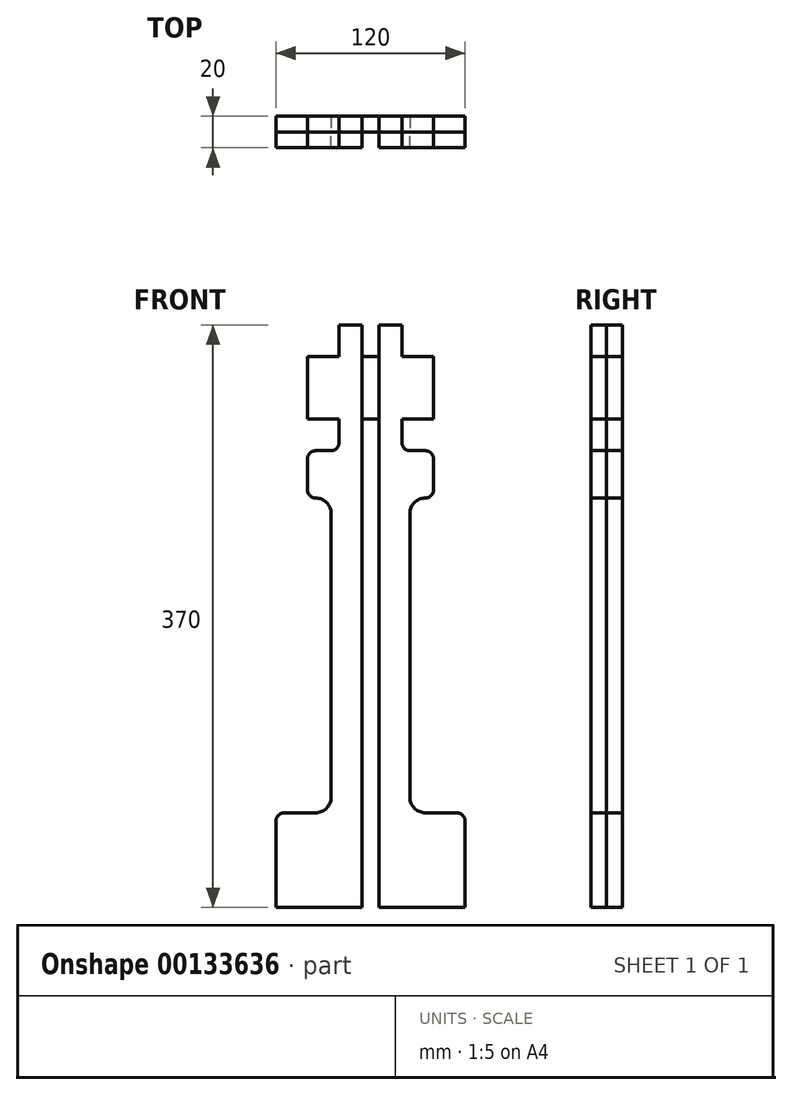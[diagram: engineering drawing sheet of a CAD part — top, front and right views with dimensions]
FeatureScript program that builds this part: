
annotation { "Feature Type Name" : "Feature", "Feature Type Description" : "" }
export const myFeature = defineFeature(function(context is Context, id is Id, definition is map)
    precondition{}
    {
        {
            var Q0;
            Q0=qCreatedBy(makeId("Front.planeOp"),FACE);
            var sketch = newSketch(context, id + "F0", { "sketchPlane" : qUnion([Q0])});
            skLineSegment(sketch, "E0.bottom", {"start": v(60, -30) * mm, "end": v(-60, -30) * mm});
            skLineSegment(sketch, "E0.top", {"start": v(55, 30) * mm, "end": v(35, 30) * mm});
            skLineSegment(sketch, "E0.left", {"start": v(60, -30) * mm, "end": v(60, 25) * mm});
            skLineSegment(sketch, "E0.right", {"start": v(-60, -30) * mm, "end": v(-60, 25) * mm});
            skPoint(sketch, "E0.middle", {"position": v(0, 0) * mm});
            skLineSegment(sketch, "E1.left", {"start": v(25, 40) * mm, "end": v(25, 220) * mm});
            skLineSegment(sketch, "E1.right", {"start": v(-25, 40) * mm, "end": v(-25, 220) * mm});
            skLineSegment(sketch, "E2.bottom", {"start": v(35, 230) * mm, "end": v(35, 230) * mm});
            skLineSegment(sketch, "E2.top", {"start": v(-25, 260) * mm, "end": v(-35, 260) * mm});
            skLineSegment(sketch, "E2.left", {"start": v(40, 235) * mm, "end": v(40, 255) * mm});
            skLineSegment(sketch, "E2.right", {"start": v(-40, 235) * mm, "end": v(-40, 255) * mm});
            skPoint(sketch, "E2.middle", {"position": v(0, 245) * mm});
            skLineSegment(sketch, "E3.top", {"start": v(20, 340) * mm, "end": v(-20, 340) * mm});
            skLineSegment(sketch, "E3.left", {"start": v(20, 265) * mm, "end": v(20, 340) * mm});
            skLineSegment(sketch, "E3.right", {"start": v(-20, 265) * mm, "end": v(-20, 340) * mm});
            skPoint(sketch, "E3.middle", {"position": v(0, 300) * mm});
            skLineSegment(sketch, "E4.bottom", {"start": v(40, 320) * mm, "end": v(-40, 320) * mm});
            skLineSegment(sketch, "E4.top", {"start": v(40, 280) * mm, "end": v(-40, 280) * mm});
            skLineSegment(sketch, "E4.left", {"start": v(40, 320) * mm, "end": v(40, 280) * mm});
            skLineSegment(sketch, "E4.right", {"start": v(-40, 320) * mm, "end": v(-40, 280) * mm});
            skLineSegment(sketch, "E5.bottom", {"start": v(5.5, -30) * mm, "end": v(-5.5, -30) * mm});
            skLineSegment(sketch, "E5.top", {"start": v(5.5, 160) * mm, "end": v(-5.5, 160) * mm});
            skLineSegment(sketch, "E5.left", {"start": v(5.5, -30) * mm, "end": v(5.5, 160) * mm});
            skLineSegment(sketch, "E5.right", {"start": v(-5.5, -30) * mm, "end": v(-5.5, 160) * mm});
            skPoint(sketch, "E5.middle", {"position": v(0, 65) * mm});
            skLineSegment(sketch, "E6.bottom", {"start": v(-5.5, 160) * mm, "end": v(5.5, 160) * mm});
            skLineSegment(sketch, "E6.top", {"start": v(-5.5, 340) * mm, "end": v(5.5, 340) * mm});
            skLineSegment(sketch, "E6.left", {"start": v(-5.5, 160) * mm, "end": v(-5.5, 340) * mm});
            skLineSegment(sketch, "E6.right", {"start": v(5.5, 160) * mm, "end": v(5.5, 340) * mm});
            skPoint(sketch, "E7.newPointA", {"position": v(-60, 30) * mm});
            skPoint(sketch, "E7.newPointB", {"position": v(25, 30) * mm});
            skArc(sketch, "E7.filletArc", {"start": v(25, 40) * mm, "mid": v(27.93, 32.93) * mm, "end": v(35, 30) * mm});
            skLineSegment(sketch, "E8", {"start": v(-55, 30) * mm, "end": v(-35, 30) * mm});
            skPoint(sketch, "E9.visualSharp", {"position": v(-25, 30) * mm});
            skArc(sketch, "E9.filletArc", {"start": v(-35, 30) * mm, "mid": v(-27.93, 32.93) * mm, "end": v(-25, 40) * mm});
            skArc(sketch, "E10.filletArc", {"start": v(-55, 30) * mm, "mid": v(-58.54, 28.54) * mm, "end": v(-60, 25) * mm});
            skPoint(sketch, "E11.visualSharp", {"position": v(60, 30) * mm});
            skArc(sketch, "E11.filletArc", {"start": v(60, 25) * mm, "mid": v(58.54, 28.54) * mm, "end": v(55, 30) * mm});
            skPoint(sketch, "E12.newPointA", {"position": v(25, 230) * mm});
            skPoint(sketch, "E12.newPointB", {"position": v(-40, 230) * mm});
            skArc(sketch, "E12.filletArc", {"start": v(35, 230) * mm, "mid": v(27.93, 227.07) * mm, "end": v(25, 220) * mm});
            skLineSegment(sketch, "E13", {"start": v(-35, 230) * mm, "end": v(-35, 230) * mm});
            skPoint(sketch, "E14.visualSharp", {"position": v(-25, 230) * mm});
            skArc(sketch, "E14.filletArc", {"start": v(-25, 220) * mm, "mid": v(-27.93, 227.07) * mm, "end": v(-35, 230) * mm});
            skPoint(sketch, "E15.newPointB", {"position": v(40, 260) * mm});
            skArc(sketch, "E15.filletArc", {"start": v(-25, 260) * mm, "mid": v(-21.46, 261.46) * mm, "end": v(-20, 265) * mm});
            skPoint(sketch, "E16.visualSharp", {"position": v(-40, 260) * mm});
            skArc(sketch, "E16.filletArc", {"start": v(-35, 260) * mm, "mid": v(-38.54, 258.54) * mm, "end": v(-40, 255) * mm});
            skArc(sketch, "E17.filletArc", {"start": v(-40, 235) * mm, "mid": v(-38.54, 231.46) * mm, "end": v(-35, 230) * mm});
            skPoint(sketch, "E18.visualSharp", {"position": v(40, 230) * mm});
            skArc(sketch, "E18.filletArc", {"start": v(35, 230) * mm, "mid": v(38.54, 231.46) * mm, "end": v(40, 235) * mm});
            skLineSegment(sketch, "E19", {"start": v(25, 260) * mm, "end": v(35, 260) * mm});
            skPoint(sketch, "E20.visualSharp", {"position": v(20, 260) * mm});
            skArc(sketch, "E20.filletArc", {"start": v(20, 265) * mm, "mid": v(21.46, 261.46) * mm, "end": v(25, 260) * mm});
            skArc(sketch, "E21.filletArc", {"start": v(40, 255) * mm, "mid": v(38.54, 258.54) * mm, "end": v(35, 260) * mm});
            skSolve(sketch);
        }
        {
            var Q0;
            {var subQ0=sQuery(id+"F0.wireOp",EDGE,"E3.right");var subQ1=sQuery(id+"F0.wireOp",EDGE,"E3.top");var subQ2=makeQuery(id+"F0.imprint","INTERSECT",VERTEX,{"derivedFrom":[subQ1,subQ0]});Q0=makeQuery(id+"F0.imprint","IMPRINT",FACE,{"disambiguationData":[TD([[makeQuery(id+"F0.imprint","IMPRINT",EDGE,{"disambiguationData":[TD([[subQ2,1.0]])],"derivedFrom":subQ0}),-1.0]])]});}
            var Q1;
            {var subQ5=sQuery(id+"F0.wireOp",EDGE,"E6.top");Q1=makeQuery(id+"F0.imprint","IMPRINT",FACE,{"disambiguationData":[TD([[makeQuery(id+"F0.imprint","IMPRINT",EDGE,{"derivedFrom":subQ5}),-1.0]])]});}
            var Q2;
            {var subQ0=sQuery(id+"F0.wireOp",EDGE,"E3.left");var subQ1=sQuery(id+"F0.wireOp",EDGE,"E3.top");var subQ2=makeQuery(id+"F0.imprint","INTERSECT",VERTEX,{"derivedFrom":[subQ1,subQ0]});Q2=makeQuery(id+"F0.imprint","IMPRINT",FACE,{"disambiguationData":[TD([[makeQuery(id+"F0.imprint","IMPRINT",EDGE,{"disambiguationData":[TD([[subQ2,1.0]])],"derivedFrom":subQ0}),1.0]])]});}
            var Q3;
            {var subQ5=sQuery(id+"F0.wireOp",EDGE,"E4.left");Q3=makeQuery(id+"F0.imprint","IMPRINT",FACE,{"disambiguationData":[TD([[makeQuery(id+"F0.imprint","IMPRINT",EDGE,{"derivedFrom":subQ5}),-1.0]])]});}
            var Q4;
            {var subQ0=sQuery(id+"F0.wireOp",EDGE,"E4.top");var subQ1=sQuery(id+"F0.wireOp",EDGE,"E3.left");var subQ2=makeQuery(id+"F0.imprint","INTERSECT",VERTEX,{"derivedFrom":[subQ1,subQ0]});Q4=makeQuery(id+"F0.imprint","IMPRINT",FACE,{"disambiguationData":[TD([[makeQuery(id+"F0.imprint","IMPRINT",EDGE,{"disambiguationData":[TD([[subQ2,-1.0]])],"derivedFrom":subQ1}),1.0]])]});}
            var Q5;
            {var subQ0=sQuery(id+"F0.wireOp",EDGE,"E6.right");var subQ1=sQuery(id+"F0.wireOp",EDGE,"E4.bottom");var subQ2=makeQuery(id+"F0.imprint","INTERSECT",VERTEX,{"derivedFrom":[subQ1,subQ0]});Q5=makeQuery(id+"F0.imprint","IMPRINT",FACE,{"disambiguationData":[TD([[makeQuery(id+"F0.imprint","IMPRINT",EDGE,{"disambiguationData":[TD([[subQ2,-1.0]])],"derivedFrom":subQ1}),1.0]])]});}
            var Q6;
            {var subQ0=sQuery(id+"F0.wireOp",EDGE,"E4.top");var subQ1=sQuery(id+"F0.wireOp",EDGE,"E3.right");var subQ2=makeQuery(id+"F0.imprint","INTERSECT",VERTEX,{"derivedFrom":[subQ1,subQ0]});Q6=makeQuery(id+"F0.imprint","IMPRINT",FACE,{"disambiguationData":[TD([[makeQuery(id+"F0.imprint","IMPRINT",EDGE,{"disambiguationData":[TD([[subQ2,-1.0]])],"derivedFrom":subQ1}),-1.0]])]});}
            var Q7;
            {var subQ5=sQuery(id+"F0.wireOp",EDGE,"E4.right");Q7=makeQuery(id+"F0.imprint","IMPRINT",FACE,{"disambiguationData":[TD([[makeQuery(id+"F0.imprint","IMPRINT",EDGE,{"derivedFrom":subQ5}),1.0]])]});}
            var Q8;
            {var subQ7=sQuery(id+"F0.wireOp",EDGE,"E0.right");Q8=makeQuery(id+"F0.imprint","IMPRINT",FACE,{"disambiguationData":[TD([[makeQuery(id+"F0.imprint","IMPRINT",EDGE,{"derivedFrom":subQ7}),-1.0]])]});}
            var Q9;
            {var subQ5=sQuery(id+"F0.wireOp",EDGE,"E6.bottom");Q9=makeQuery(id+"F0.imprint","IMPRINT",FACE,{"disambiguationData":[TD([[makeQuery(id+"F0.imprint","IMPRINT",EDGE,{"derivedFrom":subQ5}),1.0]])]});}
            var Q10;
            Q10=makeQuery(id+"F0.imprint","IMPRINT",FACE,{"disambiguationData":[TD([[makeQuery(id+"F0.imprint","IMPRINT",EDGE,{"derivedFrom":sQuery(id+"F0.wireOp",EDGE,"E0.top")}),1.0]])]});
            extrude(context, id + "F1", {"entities" : qUnion([Q0, Q1, Q2, Q3, Q4, Q5, Q6, Q7, Q8, Q9, Q10]), "oppositeDirection" : true, "depth" : 10 * mm});
        }
        {
            var Q0;
            {var subQ0=sQuery(id+"F0.wireOp",EDGE,"E3.right");var subQ1=sQuery(id+"F0.wireOp",EDGE,"E3.top");var subQ2=makeQuery(id+"F0.imprint","INTERSECT",VERTEX,{"derivedFrom":[subQ1,subQ0]});Q0=makeQuery(id+"F0.imprint","IMPRINT",FACE,{"disambiguationData":[TD([[makeQuery(id+"F0.imprint","IMPRINT",EDGE,{"disambiguationData":[TD([[subQ2,1.0]])],"derivedFrom":subQ0}),-1.0]])]});}
            var Q1;
            {var subQ0=sQuery(id+"F0.wireOp",EDGE,"E4.top");var subQ1=sQuery(id+"F0.wireOp",EDGE,"E3.right");var subQ2=makeQuery(id+"F0.imprint","INTERSECT",VERTEX,{"derivedFrom":[subQ1,subQ0]});Q1=makeQuery(id+"F0.imprint","IMPRINT",FACE,{"disambiguationData":[TD([[makeQuery(id+"F0.imprint","IMPRINT",EDGE,{"disambiguationData":[TD([[subQ2,-1.0]])],"derivedFrom":subQ1}),-1.0]])]});}
            var Q2;
            {var subQ5=sQuery(id+"F0.wireOp",EDGE,"E4.right");Q2=makeQuery(id+"F0.imprint","IMPRINT",FACE,{"disambiguationData":[TD([[makeQuery(id+"F0.imprint","IMPRINT",EDGE,{"derivedFrom":subQ5}),1.0]])]});}
            var Q3;
            {var subQ7=sQuery(id+"F0.wireOp",EDGE,"E0.right");Q3=makeQuery(id+"F0.imprint","IMPRINT",FACE,{"disambiguationData":[TD([[makeQuery(id+"F0.imprint","IMPRINT",EDGE,{"derivedFrom":subQ7}),-1.0]])]});}
            var Q4;
            Q4=makeQuery(id+"F0.imprint","IMPRINT",FACE,{"disambiguationData":[TD([[makeQuery(id+"F0.imprint","IMPRINT",EDGE,{"derivedFrom":sQuery(id+"F0.wireOp",EDGE,"E5.bottom")}),-1.0]])]});
            var Q5;
            Q5=makeQuery(id+"F0.imprint","IMPRINT",FACE,{"disambiguationData":[TD([[makeQuery(id+"F0.imprint","IMPRINT",EDGE,{"derivedFrom":sQuery(id+"F0.wireOp",EDGE,"E0.top")}),1.0]])]});
            var Q6;
            {var subQ0=sQuery(id+"F0.wireOp",EDGE,"E4.top");var subQ1=sQuery(id+"F0.wireOp",EDGE,"E3.left");var subQ2=makeQuery(id+"F0.imprint","INTERSECT",VERTEX,{"derivedFrom":[subQ1,subQ0]});Q6=makeQuery(id+"F0.imprint","IMPRINT",FACE,{"disambiguationData":[TD([[makeQuery(id+"F0.imprint","IMPRINT",EDGE,{"disambiguationData":[TD([[subQ2,-1.0]])],"derivedFrom":subQ1}),1.0]])]});}
            var Q7;
            {var subQ0=sQuery(id+"F0.wireOp",EDGE,"E3.left");var subQ1=sQuery(id+"F0.wireOp",EDGE,"E3.top");var subQ2=makeQuery(id+"F0.imprint","INTERSECT",VERTEX,{"derivedFrom":[subQ1,subQ0]});Q7=makeQuery(id+"F0.imprint","IMPRINT",FACE,{"disambiguationData":[TD([[makeQuery(id+"F0.imprint","IMPRINT",EDGE,{"disambiguationData":[TD([[subQ2,1.0]])],"derivedFrom":subQ0}),1.0]])]});}
            var Q8;
            {var subQ5=sQuery(id+"F0.wireOp",EDGE,"E4.left");Q8=makeQuery(id+"F0.imprint","IMPRINT",FACE,{"disambiguationData":[TD([[makeQuery(id+"F0.imprint","IMPRINT",EDGE,{"derivedFrom":subQ5}),-1.0]])]});}
            extrude(context, id + "F2", {"entities" : qUnion([Q0, Q1, Q2, Q3, Q4, Q5, Q6, Q7, Q8]), "depth" : 10 * mm});
        }
    });
